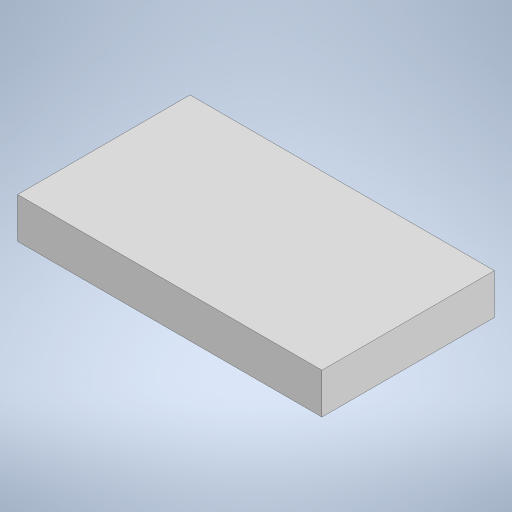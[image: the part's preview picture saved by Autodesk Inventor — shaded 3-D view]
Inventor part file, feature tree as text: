
AUTODESK INVENTOR PART (.ipt)
format: ipt  version: 2023 (Build 270158000, 158)  size: 194,048 bytes
history: native  units: mm
features: other x1, extrude x1, sketch x1
ambient origin geometry x8: Origin, YZ Plane, XZ Plane, XY Plane, X Axis, Y Axis, Z Axis, Center Point
bodies: Body1 (feature_tree)
feature tree (3):
  other  "Bryła1"
  extrude  "Wyciągnięcie proste1"  Depth=30.0mm
  sketch  "Szkic1"
